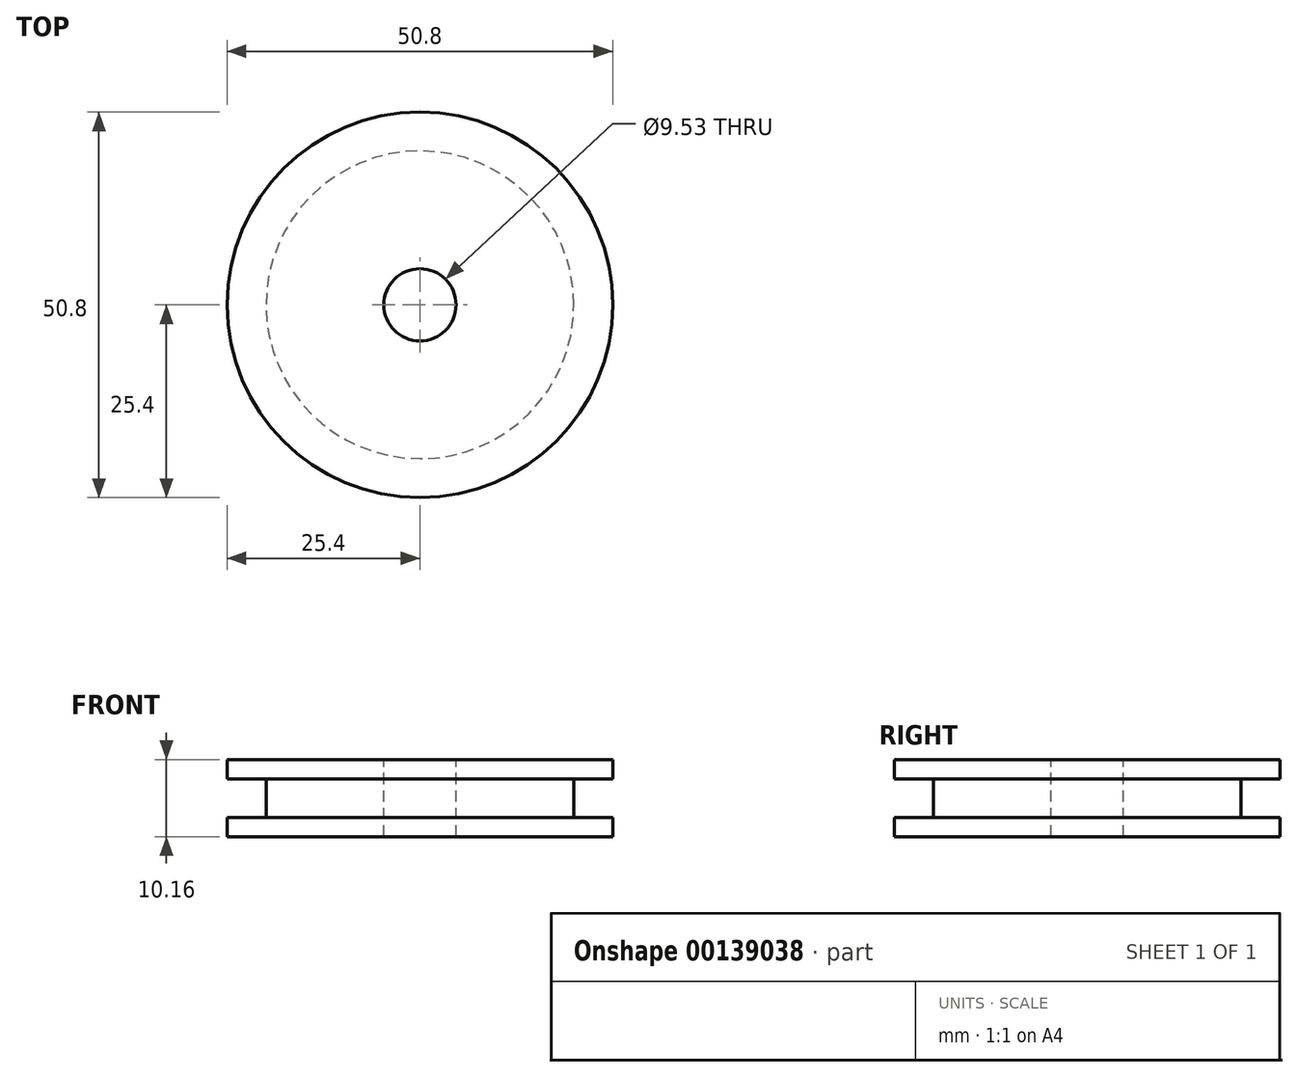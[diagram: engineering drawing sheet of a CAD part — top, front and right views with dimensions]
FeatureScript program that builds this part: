
annotation { "Feature Type Name" : "Feature", "Feature Type Description" : "" }
export const myFeature = defineFeature(function(context is Context, id is Id, definition is map)
    precondition{}
    {
        {
            var Q0;
            Q0=qCreatedBy(makeId("Front.planeOp"),FACE);
            var sketch = newSketch(context, id + "F0", { "sketchPlane" : qUnion([Q0])});
            skLineSegment(sketch, "E0", {"start": v(0, 0) * mm, "end": v(0, 10.16) * mm});
            skLineSegment(sketch, "E1", {"start": v(0, 2.54) * mm, "end": v(-25.4, 2.54) * mm});
            skLineSegment(sketch, "E2", {"start": v(-25.4, 2.54) * mm, "end": v(-25.4, 0) * mm});
            skLineSegment(sketch, "E3", {"start": v(-25.4, 0) * mm, "end": v(0, 0) * mm});
            skLineSegment(sketch, "E4", {"start": v(0, 7.62) * mm, "end": v(-25.4, 7.62) * mm});
            skLineSegment(sketch, "E5", {"start": v(0, 10.16) * mm, "end": v(-25.4, 10.16) * mm});
            skLineSegment(sketch, "E6", {"start": v(-25.4, 7.62) * mm, "end": v(-25.4, 10.16) * mm});
            skLineSegment(sketch, "E7", {"start": v(-20.27, 2.54) * mm, "end": v(-20.27, 7.62) * mm});
            skSolve(sketch);
        }
        {
            var Q0;
            {var subQ5=sQuery(id+"F0.wireOp",EDGE,"E7");Q0=makeQuery(id+"F0.imprint","IMPRINT",FACE,{"disambiguationData":[TD([[makeQuery(id+"F0.imprint","IMPRINT",EDGE,{"derivedFrom":subQ5}),-1.0]])]});}
            var Q1;
            {var subQ0=sQuery(id+"F0.wireOp",EDGE,"E5");Q1=makeQuery(id+"F0.imprint","IMPRINT",FACE,{"disambiguationData":[TD([[makeQuery(id+"F0.imprint","IMPRINT",EDGE,{"derivedFrom":subQ0}),1.0]])]});}
            var Q2;
            {var subQ0=sQuery(id+"F0.wireOp",EDGE,"E2");Q2=makeQuery(id+"F0.imprint","IMPRINT",FACE,{"disambiguationData":[TD([[makeQuery(id+"F0.imprint","IMPRINT",EDGE,{"derivedFrom":subQ0}),1.0]])]});}
            var Q3;
            Q3=sQuery(id+"F0.wireOp",EDGE,"E0");
            revolve(context, id + "F1", {"entities" : qUnion([Q0, Q1, Q2]), "axis" : qUnion([Q3]), "revolveType" : RevolveType.FULL});
        }
        {
            var Q0;
            Q0=makeQuery(id+"F1.opRevolve","SWEPT_FACE",FACE,{"disambiguationData":[OSD([sQuery(id+"F0.wireOp",EDGE,"E5")])]});
            var sketch = newSketch(context, id + "F2", { "sketchPlane" : qUnion([Q0])});
            skCircle(sketch, "E8", {"center": v(0, 0) * mm, "radius": 3.18 * mm});
            skSolve(sketch);
        }
        {
            var Q0;
            Q0=sQuery(id+"F2.wireOp",VERTEX,"E8.center");
            var Q1;
            Q1=makeQuery(id+"F1.opRevolve","SWEPT_BODY",BODY,{"disambiguationData":[OSD([sQuery(id+"F0.wireOp",EDGE,"E0"),sQuery(id+"F0.wireOp",EDGE,"E1"),sQuery(id+"F0.wireOp",EDGE,"E2"),sQuery(id+"F0.wireOp",EDGE,"E3"),sQuery(id+"F0.wireOp",EDGE,"E4"),sQuery(id+"F0.wireOp",EDGE,"E5"),sQuery(id+"F0.wireOp",EDGE,"E6"),sQuery(id+"F0.wireOp",EDGE,"E7")])]});
            hole(context, id + "F3", {"style" : HoleStyle.SIMPLE, "endStyle" : HoleEndStyle.BLIND, "holeDiameter" : 9.52 * mm, "holeDepth" : 50.8 * mm, "locations" : qUnion([Q0]), "scope" : qUnion([Q1])});
        }
    });
